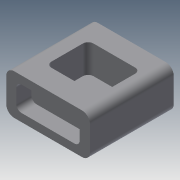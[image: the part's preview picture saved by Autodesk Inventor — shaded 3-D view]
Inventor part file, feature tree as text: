
AUTODESK INVENTOR PART (.ipt)
format: ipt  version: 2015 (Build 190159000, 159)  size: 148,992 bytes
history: native  units: in
note: dims shown in document units (in); Inventor stores cm internally (conversion verified against a paired STEP export)
features: extrude x4, sketch x4
ambient origin geometry x8: Origin, YZ Plane, XZ Plane, XY Plane, X Axis, Y Axis, Z Axis, Center Point
bodies: Solid1 (feature_tree)
feature tree (8):
  extrude  "Extrusion1"  Depth=1.53in
  extrude  "Extrusion2"  Depth=0.3in
  extrude  "Extrusion3"  Depth=0.3in
  extrude  "Extrusion4"  Depth=1.59in
  sketch  "Sketch1"  dims[d0=3.17in d1=1.53in]
  sketch  "Sketch2"  dims[d2=0.3in d3=0.3in]
  sketch  "Sketch3"  dims[d4=0.3in d5=0.3in]
  sketch  "Sketch4"  dims[d14=3.17in d15=0.0in d16=1.59in d17=1.98in d18=0.82in d19=0.5in d20=0.2in d21=0.2in d22=0.2in d23=0.2in d24=1.07in d25=0.0in d26=2.4in d27=0.39in d28=0.93in d29=0.3in d30=0.2in d31=0.2in d32=0.57in d33=0.0in d34=2.5in d35=1.0in d36=0.34in d37=0.27in d38=0.2in d39=0.57in d40=0.0in]
